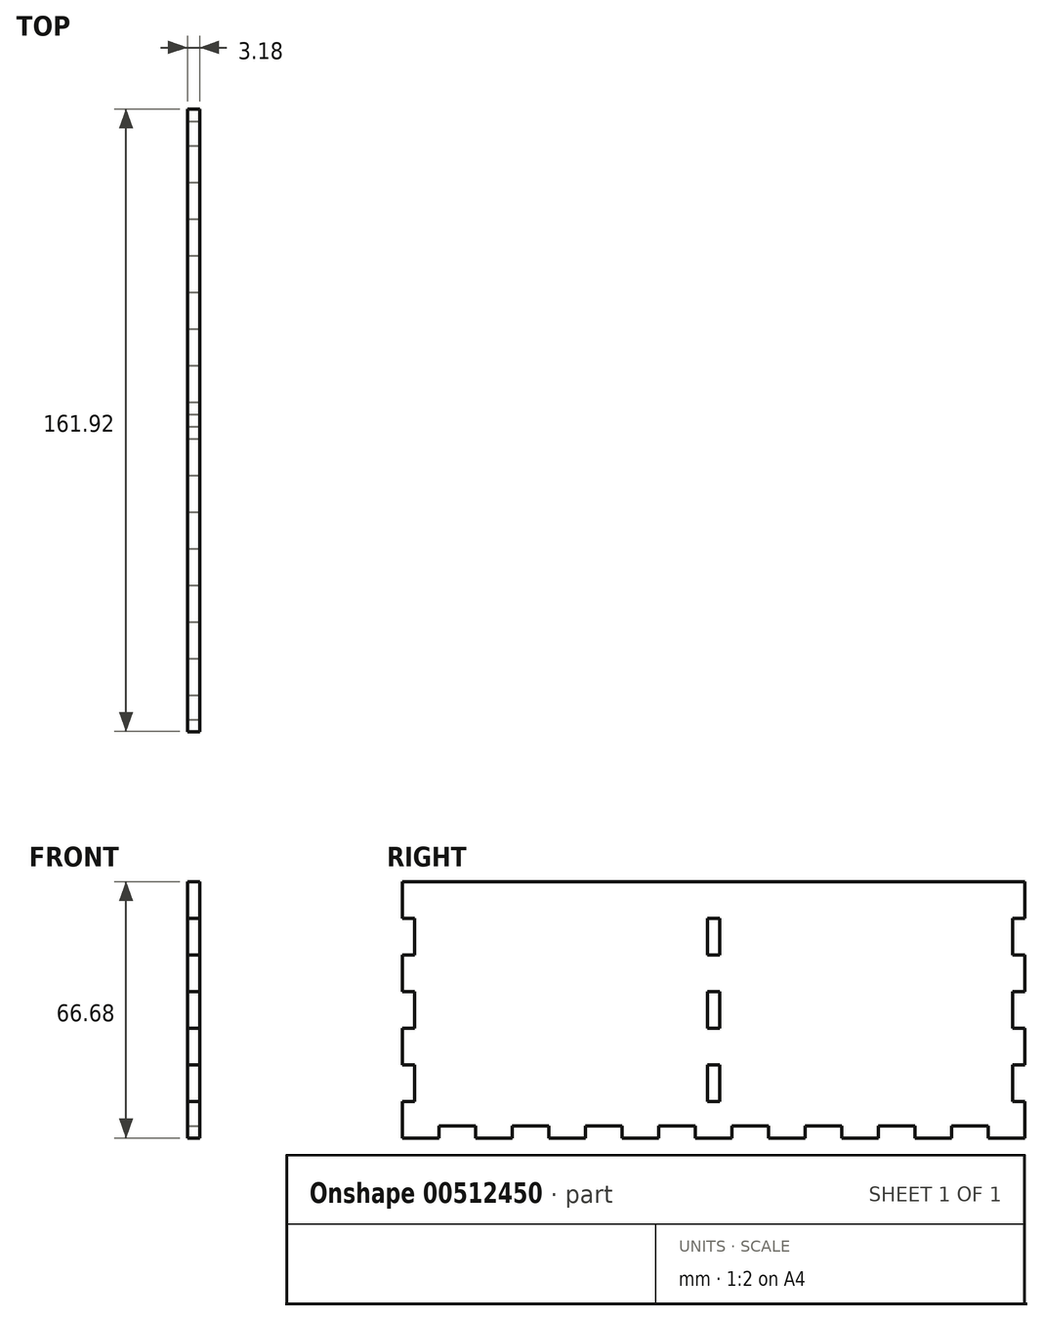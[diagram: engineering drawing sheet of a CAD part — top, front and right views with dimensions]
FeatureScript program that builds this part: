
annotation { "Feature Type Name" : "Feature", "Feature Type Description" : "" }
export const myFeature = defineFeature(function(context is Context, id is Id, definition is map)
    precondition{}
    {
        {
            var Q0;
            Q0=qCreatedBy(makeId("Right.planeOp"),FACE);
            var sketch = newSketch(context, id + "F0", { "sketchPlane" : qUnion([Q0])});
            skLineSegment(sketch, "E0.bottom", {"start": v(-80.96, 33.34) * mm, "end": v(80.96, 33.34) * mm});
            skLineSegment(sketch, "E0.top", {"start": v(-80.96, -33.34) * mm, "end": v(80.96, -33.34) * mm});
            skLineSegment(sketch, "E0.left", {"start": v(-80.96, 33.34) * mm, "end": v(-80.96, -33.34) * mm});
            skLineSegment(sketch, "E0.right", {"start": v(80.96, 33.34) * mm, "end": v(80.96, -33.34) * mm});
            skSolve(sketch);
        }
        {
            var Q0;
            Q0=makeQuery(id+"F0.imprint","IMPRINT",FACE,{"disambiguationData":[TD([[makeQuery(id+"F0.imprint","IMPRINT",EDGE,{"derivedFrom":sQuery(id+"F0.wireOp",EDGE,"E0.bottom")}),-1.0]])]});
            extrude(context, id + "F1", {"entities" : qUnion([Q0]), "depth" : 3.17 * mm});
        }
        {
            var Q0;
            Q0=makeQuery(id+"F1.opExtrude","CAP_FACE",FACE,{"disambiguationData":[OSD([sQuery(id+"F0.wireOp",EDGE,"E0.bottom"),sQuery(id+"F0.wireOp",EDGE,"E0.top"),sQuery(id+"F0.wireOp",EDGE,"E0.left"),sQuery(id+"F0.wireOp",EDGE,"E0.right")])],"isStart":false});
            var sketch = newSketch(context, id + "F2", { "sketchPlane" : qUnion([Q0])});
            skLineSegment(sketch, "E1.bottom", {"start": v(-80.96, -23.81) * mm, "end": v(-77.79, -23.81) * mm});
            skLineSegment(sketch, "E1.top", {"start": v(-80.96, -14.29) * mm, "end": v(-77.79, -14.29) * mm});
            skLineSegment(sketch, "E1.left", {"start": v(-80.96, -23.81) * mm, "end": v(-80.96, -14.29) * mm});
            skLineSegment(sketch, "E1.right", {"start": v(-77.79, -23.81) * mm, "end": v(-77.79, -14.29) * mm});
            skLineSegment(sketch, "E2.0.1.0", {"start": v(-77.79, -4.76) * mm, "end": v(-77.79, 4.76) * mm});
            skLineSegment(sketch, "E2.0.1.1", {"start": v(-80.96, -4.76) * mm, "end": v(-80.96, 4.76) * mm});
            skLineSegment(sketch, "E2.0.1.2", {"start": v(-80.96, -4.76) * mm, "end": v(-77.79, -4.76) * mm});
            skLineSegment(sketch, "E2.0.1.3", {"start": v(-80.96, 4.76) * mm, "end": v(-77.79, 4.76) * mm});
            skLineSegment(sketch, "E2.0.2.0", {"start": v(-77.79, 14.29) * mm, "end": v(-77.79, 23.81) * mm});
            skLineSegment(sketch, "E2.0.2.1", {"start": v(-80.96, 14.29) * mm, "end": v(-80.96, 23.81) * mm});
            skLineSegment(sketch, "E2.0.2.2", {"start": v(-80.96, 14.29) * mm, "end": v(-77.79, 14.29) * mm});
            skLineSegment(sketch, "E2.0.2.3", {"start": v(-80.96, 23.81) * mm, "end": v(-77.79, 23.81) * mm});
            skLineSegment(sketch, "E2.direction1", {"start": v(-80.96, -23.81) * mm, "end": v(-1.59, -23.81) * mm, "construction": true});
            skLineSegment(sketch, "E2.direction2", {"start": v(-80.96, -23.81) * mm, "end": v(-80.96, -4.76) * mm, "construction": true});
            skLineSegment(sketch, "E3.0.1.0", {"start": v(1.59, -23.81) * mm, "end": v(1.59, -14.29) * mm});
            skLineSegment(sketch, "E3.3.1.0", {"start": v(-1.59, -23.81) * mm, "end": v(-1.59, -14.29) * mm});
            skLineSegment(sketch, "E3.6.1.0", {"start": v(-1.59, -23.81) * mm, "end": v(1.59, -23.81) * mm});
            skLineSegment(sketch, "E3.9.1.0", {"start": v(-1.59, -14.29) * mm, "end": v(1.59, -14.29) * mm});
            skLineSegment(sketch, "E3.0.1.1", {"start": v(1.59, -4.76) * mm, "end": v(1.59, 4.76) * mm});
            skLineSegment(sketch, "E3.3.1.1", {"start": v(-1.59, -4.76) * mm, "end": v(-1.59, 4.76) * mm});
            skLineSegment(sketch, "E3.6.1.1", {"start": v(-1.59, -4.76) * mm, "end": v(1.59, -4.76) * mm});
            skLineSegment(sketch, "E3.9.1.1", {"start": v(-1.59, 4.76) * mm, "end": v(1.59, 4.76) * mm});
            skLineSegment(sketch, "E3.0.1.2", {"start": v(1.59, 14.29) * mm, "end": v(1.59, 23.81) * mm});
            skLineSegment(sketch, "E3.3.1.2", {"start": v(-1.59, 14.29) * mm, "end": v(-1.59, 23.81) * mm});
            skLineSegment(sketch, "E3.6.1.2", {"start": v(-1.59, 14.29) * mm, "end": v(1.59, 14.29) * mm});
            skLineSegment(sketch, "E3.9.1.2", {"start": v(-1.59, 23.81) * mm, "end": v(1.59, 23.81) * mm});
            skLineSegment(sketch, "E4.0.2.0", {"start": v(80.96, -23.81) * mm, "end": v(80.96, -14.29) * mm});
            skLineSegment(sketch, "E4.3.2.0", {"start": v(77.79, -23.81) * mm, "end": v(77.79, -14.29) * mm});
            skLineSegment(sketch, "E4.6.2.0", {"start": v(77.79, -23.81) * mm, "end": v(80.96, -23.81) * mm});
            skLineSegment(sketch, "E4.9.2.0", {"start": v(77.79, -14.29) * mm, "end": v(80.96, -14.29) * mm});
            skLineSegment(sketch, "E4.0.2.1", {"start": v(80.96, -4.76) * mm, "end": v(80.96, 4.76) * mm});
            skLineSegment(sketch, "E4.3.2.1", {"start": v(77.79, -4.76) * mm, "end": v(77.79, 4.76) * mm});
            skLineSegment(sketch, "E4.6.2.1", {"start": v(77.79, -4.76) * mm, "end": v(80.96, -4.76) * mm});
            skLineSegment(sketch, "E4.9.2.1", {"start": v(77.79, 4.76) * mm, "end": v(80.96, 4.76) * mm});
            skLineSegment(sketch, "E4.0.2.2", {"start": v(80.96, 14.29) * mm, "end": v(80.96, 23.81) * mm});
            skLineSegment(sketch, "E4.3.2.2", {"start": v(77.79, 14.29) * mm, "end": v(77.79, 23.81) * mm});
            skLineSegment(sketch, "E4.6.2.2", {"start": v(77.79, 14.29) * mm, "end": v(80.96, 14.29) * mm});
            skLineSegment(sketch, "E4.9.2.2", {"start": v(77.79, 23.81) * mm, "end": v(80.96, 23.81) * mm});
            skSolve(sketch);
        }
        {
            var Q0;
            Q0 = qSketchRegion(id + "F2", true);
            extrude(context, id + "F3", {"entities" : qUnion([Q0]), "operationType" : NewBodyOperationType.REMOVE, "endBound" : BoundingType.THROUGH_ALL, "oppositeDirection" : true, "depth" : 25.4 * mm});
        }
        {
            var Q0;
            Q0=makeQuery(id+"F1.opExtrude","CAP_FACE",FACE,{"disambiguationData":[OSD([sQuery(id+"F0.wireOp",EDGE,"E0.bottom"),sQuery(id+"F0.wireOp",EDGE,"E0.top"),sQuery(id+"F0.wireOp",EDGE,"E0.left"),sQuery(id+"F0.wireOp",EDGE,"E0.right")])],"isStart":false});
            var sketch = newSketch(context, id + "F4", { "sketchPlane" : qUnion([Q0])});
            skLineSegment(sketch, "E5.bottom", {"start": v(-71.44, -33.34) * mm, "end": v(-61.91, -33.34) * mm});
            skLineSegment(sketch, "E5.top", {"start": v(-71.44, -30.16) * mm, "end": v(-61.91, -30.16) * mm});
            skLineSegment(sketch, "E5.left", {"start": v(-71.44, -33.34) * mm, "end": v(-71.44, -30.16) * mm});
            skLineSegment(sketch, "E5.right", {"start": v(-61.91, -33.34) * mm, "end": v(-61.91, -30.16) * mm});
            skLineSegment(sketch, "E6.1.0.0", {"start": v(-42.86, -33.34) * mm, "end": v(-42.86, -30.16) * mm});
            skLineSegment(sketch, "E6.1.0.1", {"start": v(-52.39, -33.34) * mm, "end": v(-52.39, -30.16) * mm});
            skLineSegment(sketch, "E6.1.0.2", {"start": v(-52.39, -30.16) * mm, "end": v(-42.86, -30.16) * mm});
            skLineSegment(sketch, "E6.1.0.3", {"start": v(-52.39, -33.34) * mm, "end": v(-42.86, -33.34) * mm});
            skLineSegment(sketch, "E6.2.0.0", {"start": v(-23.81, -33.34) * mm, "end": v(-23.81, -30.16) * mm});
            skLineSegment(sketch, "E6.2.0.1", {"start": v(-33.34, -33.34) * mm, "end": v(-33.34, -30.16) * mm});
            skLineSegment(sketch, "E6.2.0.2", {"start": v(-33.34, -30.16) * mm, "end": v(-23.81, -30.16) * mm});
            skLineSegment(sketch, "E6.2.0.3", {"start": v(-33.34, -33.34) * mm, "end": v(-23.81, -33.34) * mm});
            skLineSegment(sketch, "E6.3.0.0", {"start": v(-4.76, -33.34) * mm, "end": v(-4.76, -30.16) * mm});
            skLineSegment(sketch, "E6.3.0.1", {"start": v(-14.29, -33.34) * mm, "end": v(-14.29, -30.16) * mm});
            skLineSegment(sketch, "E6.3.0.2", {"start": v(-14.29, -30.16) * mm, "end": v(-4.76, -30.16) * mm});
            skLineSegment(sketch, "E6.3.0.3", {"start": v(-14.29, -33.34) * mm, "end": v(-4.76, -33.34) * mm});
            skLineSegment(sketch, "E6.4.0.0", {"start": v(14.29, -33.34) * mm, "end": v(14.29, -30.16) * mm});
            skLineSegment(sketch, "E6.4.0.1", {"start": v(4.76, -33.34) * mm, "end": v(4.76, -30.16) * mm});
            skLineSegment(sketch, "E6.4.0.2", {"start": v(4.76, -30.16) * mm, "end": v(14.29, -30.16) * mm});
            skLineSegment(sketch, "E6.4.0.3", {"start": v(4.76, -33.34) * mm, "end": v(14.29, -33.34) * mm});
            skLineSegment(sketch, "E6.5.0.0", {"start": v(33.34, -33.34) * mm, "end": v(33.34, -30.16) * mm});
            skLineSegment(sketch, "E6.5.0.1", {"start": v(23.81, -33.34) * mm, "end": v(23.81, -30.16) * mm});
            skLineSegment(sketch, "E6.5.0.2", {"start": v(23.81, -30.16) * mm, "end": v(33.34, -30.16) * mm});
            skLineSegment(sketch, "E6.5.0.3", {"start": v(23.81, -33.34) * mm, "end": v(33.34, -33.34) * mm});
            skLineSegment(sketch, "E6.6.0.0", {"start": v(52.39, -33.34) * mm, "end": v(52.39, -30.16) * mm});
            skLineSegment(sketch, "E6.6.0.1", {"start": v(42.86, -33.34) * mm, "end": v(42.86, -30.16) * mm});
            skLineSegment(sketch, "E6.6.0.2", {"start": v(42.86, -30.16) * mm, "end": v(52.39, -30.16) * mm});
            skLineSegment(sketch, "E6.6.0.3", {"start": v(42.86, -33.34) * mm, "end": v(52.39, -33.34) * mm});
            skLineSegment(sketch, "E6.7.0.0", {"start": v(71.44, -33.34) * mm, "end": v(71.44, -30.16) * mm});
            skLineSegment(sketch, "E6.7.0.1", {"start": v(61.91, -33.34) * mm, "end": v(61.91, -30.16) * mm});
            skLineSegment(sketch, "E6.7.0.2", {"start": v(61.91, -30.16) * mm, "end": v(71.44, -30.16) * mm});
            skLineSegment(sketch, "E6.7.0.3", {"start": v(61.91, -33.34) * mm, "end": v(71.44, -33.34) * mm});
            skLineSegment(sketch, "E6.direction1", {"start": v(-71.44, -33.34) * mm, "end": v(-52.39, -33.34) * mm, "construction": true});
            skSolve(sketch);
        }
        {
            var Q0;
            Q0 = qSketchRegion(id + "F4", true);
            extrude(context, id + "F5", {"entities" : qUnion([Q0]), "operationType" : NewBodyOperationType.REMOVE, "endBound" : BoundingType.THROUGH_ALL, "oppositeDirection" : true, "depth" : 25.4 * mm});
        }
    });
